# Revit family: Lüftungsrohrschelle, Ø630mm, ohne AG, Gummi
name_source: partatom
category: HLS-Bauteile
revit_build: Autodesk Revit 2018 (Build: 20190510_1515(x64)
units: mm (PartAtom-declared; Revit-internal decimal feet)

## family parameters
Arbeitsebenenbasiert = Ja
Beim Laden mit Abzugskörper schneiden = Nein
Bemaßung runder Anschluss = Durchmesser verwenden
Gemeinsam genutzt = Ja
Immer vertikal = Nein
Raumberechnungspunkt = Nein
Teiletyp = Normal

## types (1)
- Lüftungsrohrschelle, o.AG, o.VS, DN 630, Gummi
    A = 0 mm  [stored 0 ft]
    AB = 4 mm  [stored 0.0131234 ft]
    Achsabstand = 686 mm
    Anschluss = ohne Anschluss
    Artikelnummer = 0436300
    B = 711 mm
    Bauart = zweiteilig
    Baustoffklasse = B2
    Breite = 676 mm
    Breite Material = 25 mm
    D = 635 mm
    D0 = 647 mm  [stored 2.1227 ft]
    DF1 = 25 mm  [stored 0.082021 ft]
    DF2 = 35 mm
    DS = 6 mm  [stored 0.019685 ft]
    DVS = 10 mm  [stored 0.0328084 ft]
    Dämmstärke = 6 mm  [stored 0.019685 ft]
    EAN = 4250928410528
    Fabrikat = MEFA
    Farbe Schalldämmeinlage = Schwarz
    Firma = MEFA Befestigungs- und Montagesysteme GmbH
    Gewicht = 1.60 kg
    Gewicht pro Bauteil = 1.60 kg
    H = 657 mm
    HGA = 0 mm  [stored 0 ft]
    Höhe = 657 mm
    Kurztext1 = Lüftungsschelle Standard 25x3
    Kurztext2 = DN 630 ohne Anschluss TPE
    Lochdurchmesser = 10.5 mm
    MB = 25 mm  [stored 0.082021 ft]
    MD = 3 mm  [stored 0.00984252 ft]
    Material = Stahl
    Material Schalldämmeinlage = TPE
    Materialmaße = 25x2,5 mm
    Materialname = S235
    Mengeneinheit = St
    Nennweite DN Rohr = 630 mm
    Oberflaeche = feuerbandverzinkt
    R = 324 mm
    RM = 327 mm
    Rohraußendurchmesser = 635 mm
    Rohraußendurchmesser Zoll = Zoll
    S = 686 mm
    Schalldämmeinlage = Gummi TPE
    Stärke Material = 3 mm  [stored 0.00984252 ft]
    Verschluss = Mutter / Verschluss-Schraube
    Vorgabe-Ansicht = 1219 mm
    max. Höhe = 621 mm
    max. Rohraußendurchmesser = 0 mm  [stored 0 ft]
    max. Temperaturbeständigkeit = +100 °C
    max. zul. Last = 2.00 kN
    max. zul. Last horizontal = 0.00 kN
    max. zul. Last vertikal = 0.00 kN
    min. Rohraußendurchmesser = 0 mm  [stored 0 ft]
    vpe = 1

note: [stored X ft] marks values corroborated as IEEE doubles in the binary element streams (Revit-internal decimal feet)

## geometry (parser evidence)
native form markers: Sweep x7
no freeform markers — native parametric forms only
